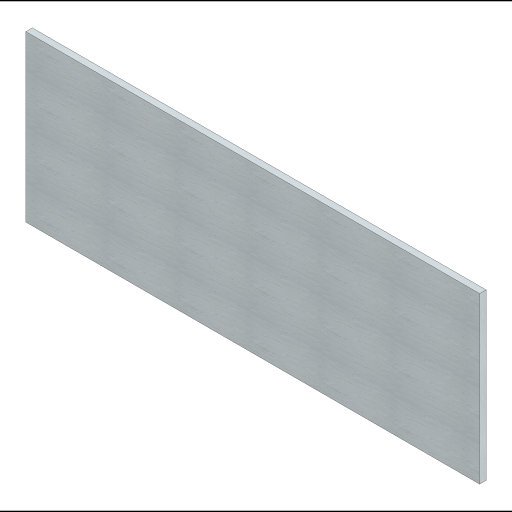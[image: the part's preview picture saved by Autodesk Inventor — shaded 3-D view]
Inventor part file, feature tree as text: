
AUTODESK INVENTOR PART (.ipt)
format: ipt  version: 2023 (Build 270158000, 158)  size: 253,952 bytes
history: native  units: in
note: dims shown in document units (in); Inventor stores cm internally (conversion verified against a paired STEP export)
features: extrude x1, sketch x1
ambient origin geometry x8: Origin, YZ Plane, XZ Plane, XY Plane, X Axis, Y Axis, Z Axis, Center Point
bodies: Solid1 (feature_tree)
feature tree (2):
  extrude  "Extrusion1"  Depth=33.0in
  sketch  "Sketch1"  dims[d0=12.0in d1=33.0in d2=0.47in d3=0.0in]
